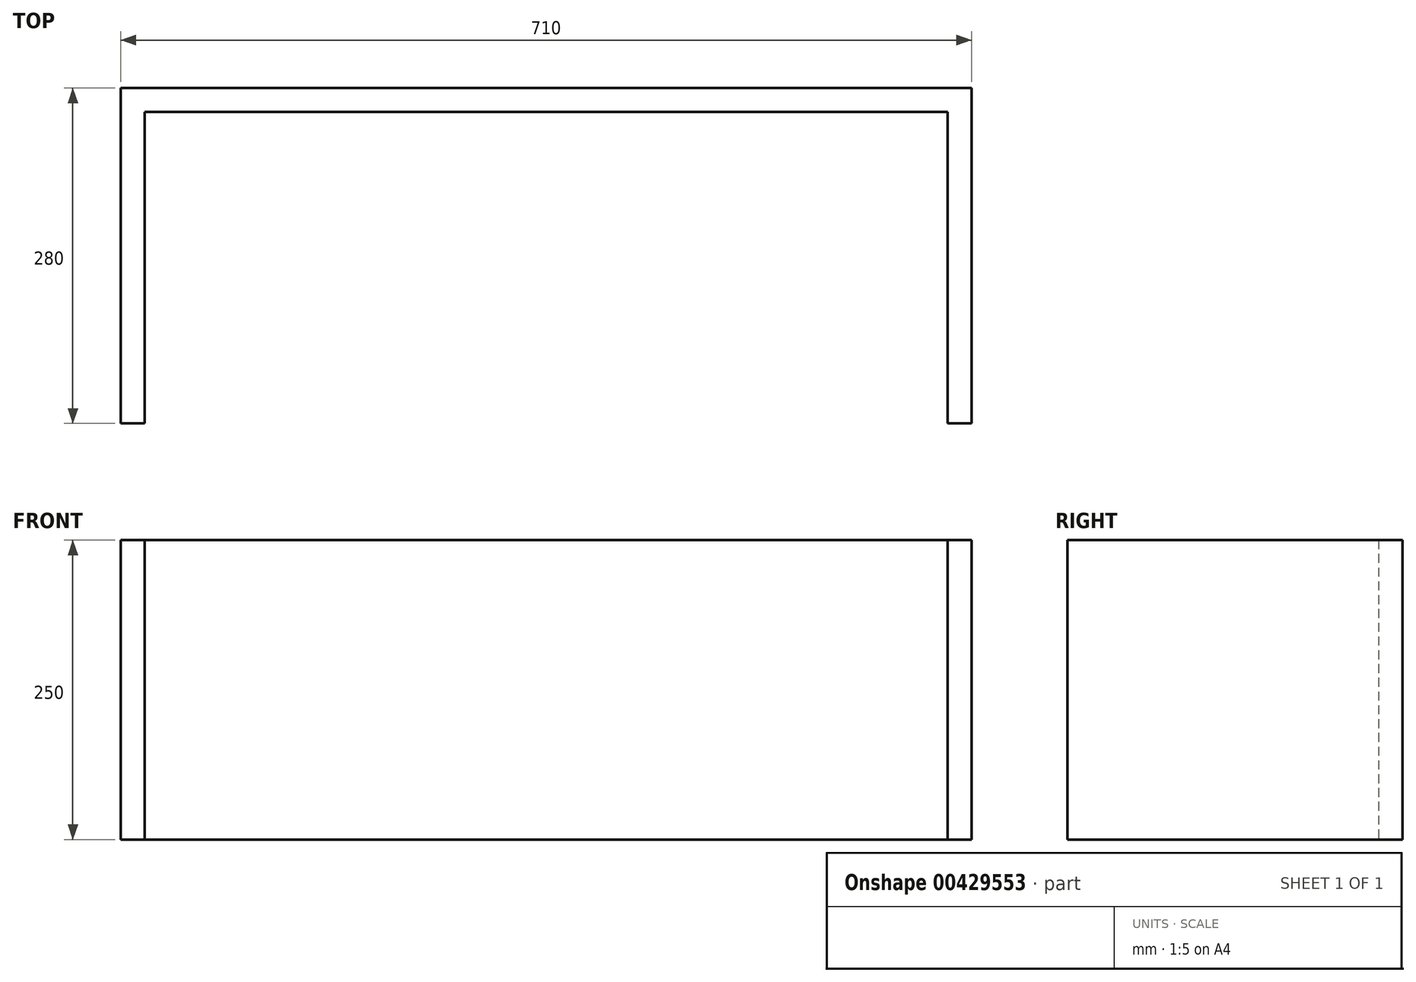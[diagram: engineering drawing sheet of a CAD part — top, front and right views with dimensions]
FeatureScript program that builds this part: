
annotation { "Feature Type Name" : "Feature", "Feature Type Description" : "" }
export const myFeature = defineFeature(function(context is Context, id is Id, definition is map)
    precondition{}
    {
        {
            var Q0;
            Q0=qCreatedBy(makeId("Top.planeOp"),FACE);
            var sketch = newSketch(context, id + "F0", { "sketchPlane" : qUnion([Q0])});
            skLineSegment(sketch, "E0.bottom", {"start": v(355, -150) * mm, "end": v(-355, -150) * mm});
            skLineSegment(sketch, "E0.top", {"start": v(355, 150) * mm, "end": v(-355, 150) * mm});
            skLineSegment(sketch, "E0.left", {"start": v(355, -150) * mm, "end": v(355, 150) * mm});
            skLineSegment(sketch, "E0.right", {"start": v(-355, -150) * mm, "end": v(-355, 150) * mm});
            skPoint(sketch, "E0.middle", {"position": v(0, 0) * mm});
            skLineSegment(sketch, "E1.0", {"start": v(-335, -150) * mm, "end": v(-335, 150) * mm});
            skLineSegment(sketch, "E2.0", {"start": v(355, 130) * mm, "end": v(-355, 130) * mm});
            skLineSegment(sketch, "E3.0", {"start": v(335, -150) * mm, "end": v(335, 150) * mm});
            skLineSegment(sketch, "E4.0", {"start": v(355, -130) * mm, "end": v(-355, -130) * mm});
            skSolve(sketch);
        }
        {
            var Q0;
            {var subQ0=sQuery(id+"F0.wireOp",EDGE,"E0.left");var subQ1=sQuery(id+"F0.wireOp",EDGE,"E0.top");var subQ2=makeQuery(id+"F0.imprint","INTERSECT",VERTEX,{"derivedFrom":[subQ1,subQ0]});Q0=makeQuery(id+"F0.imprint","IMPRINT",FACE,{"disambiguationData":[TD([[makeQuery(id+"F0.imprint","IMPRINT",EDGE,{"disambiguationData":[TD([[subQ2,-1.0]])],"derivedFrom":subQ1}),1.0]])]});}
            var Q1;
            {var subQ0=sQuery(id+"F0.wireOp",EDGE,"E0.right");var subQ1=sQuery(id+"F0.wireOp",EDGE,"E0.top");var subQ2=makeQuery(id+"F0.imprint","INTERSECT",VERTEX,{"derivedFrom":[subQ1,subQ0]});Q1=makeQuery(id+"F0.imprint","IMPRINT",FACE,{"disambiguationData":[TD([[makeQuery(id+"F0.imprint","IMPRINT",EDGE,{"disambiguationData":[TD([[subQ2,1.0]])],"derivedFrom":subQ1}),1.0]])]});}
            var Q2;
            {var subQ0=sQuery(id+"F0.wireOp",EDGE,"E1.0");var subQ1=sQuery(id+"F0.wireOp",EDGE,"E0.top");var subQ2=makeQuery(id+"F0.imprint","INTERSECT",VERTEX,{"derivedFrom":[subQ1,subQ0]});Q2=makeQuery(id+"F0.imprint","IMPRINT",FACE,{"disambiguationData":[TD([[makeQuery(id+"F0.imprint","IMPRINT",EDGE,{"disambiguationData":[TD([[subQ2,1.0]])],"derivedFrom":subQ1}),1.0]])]});}
            var Q3;
            {var subQ0=sQuery(id+"F0.wireOp",EDGE,"E2.0");var subQ1=sQuery(id+"F0.wireOp",EDGE,"E0.left");var subQ2=makeQuery(id+"F0.imprint","INTERSECT",VERTEX,{"derivedFrom":[subQ1,subQ0]});Q3=makeQuery(id+"F0.imprint","IMPRINT",FACE,{"disambiguationData":[TD([[makeQuery(id+"F0.imprint","IMPRINT",EDGE,{"disambiguationData":[TD([[subQ2,1.0]])],"derivedFrom":subQ1}),1.0]])]});}
            var Q4;
            {var subQ0=sQuery(id+"F0.wireOp",EDGE,"E2.0");var subQ1=sQuery(id+"F0.wireOp",EDGE,"E0.right");var subQ2=makeQuery(id+"F0.imprint","INTERSECT",VERTEX,{"derivedFrom":[subQ1,subQ0]});Q4=makeQuery(id+"F0.imprint","IMPRINT",FACE,{"disambiguationData":[TD([[makeQuery(id+"F0.imprint","IMPRINT",EDGE,{"disambiguationData":[TD([[subQ2,1.0]])],"derivedFrom":subQ1}),-1.0]])]});}
            extrude(context, id + "F1", {"entities" : qUnion([Q0, Q1, Q2, Q3, Q4]), "depth" : 250 * mm});
        }
    });
